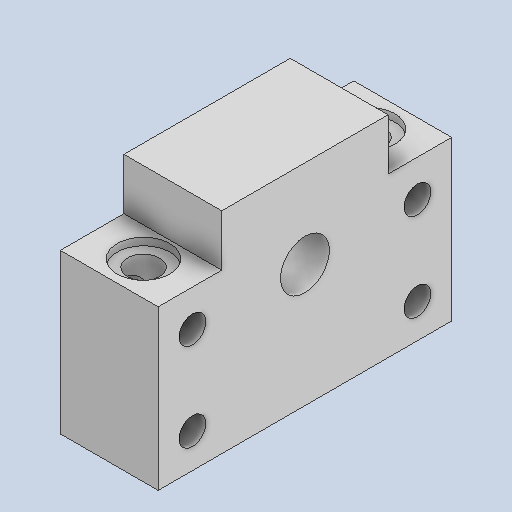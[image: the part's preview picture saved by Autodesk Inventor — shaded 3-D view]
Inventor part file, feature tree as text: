
AUTODESK INVENTOR PART (.ipt)
format: ipt  version: 2023 (Build 270158000, 158)  size: 199,168 bytes
history: native  units: mm
features: extrude x4, sketch x4
ambient origin geometry x8: Origin, YZ Plane, XZ Plane, XY Plane, X Axis, Y Axis, Z Axis, Center Point
bodies: Solid1 (feature_tree)
feature tree (8):
  extrude  "Extrusion1"  Depth=60.0mm
  extrude  "Extrusion2"  Depth=32.5mm
  extrude  "Extrusion3"  Depth=25.0mm
  extrude  "Extrusion4"  Depth=10.0mm
  sketch  "Sketch1"  dims[d0=34.0mm d1=60.0mm]
  sketch  "Sketch2"  dims[d2=43.0mm d3=32.5mm]
  sketch  "Sketch3"  dims[d4=5.5mm d6=25.0mm]
  sketch  "Sketch4"  dims[d7=18.0mm d8=46.0mm d9=10.0mm d10=20.0mm d11=0.0mm d12=10.8mm d13=10.8mm d14=46.0mm d15=7.0mm d16=10.0mm d17=1.5mm d18=0.0mm d19=6.6mm d20=5.0mm d21=0.0mm d22=22.0mm d23=10.0mm d24=0.0mm]
